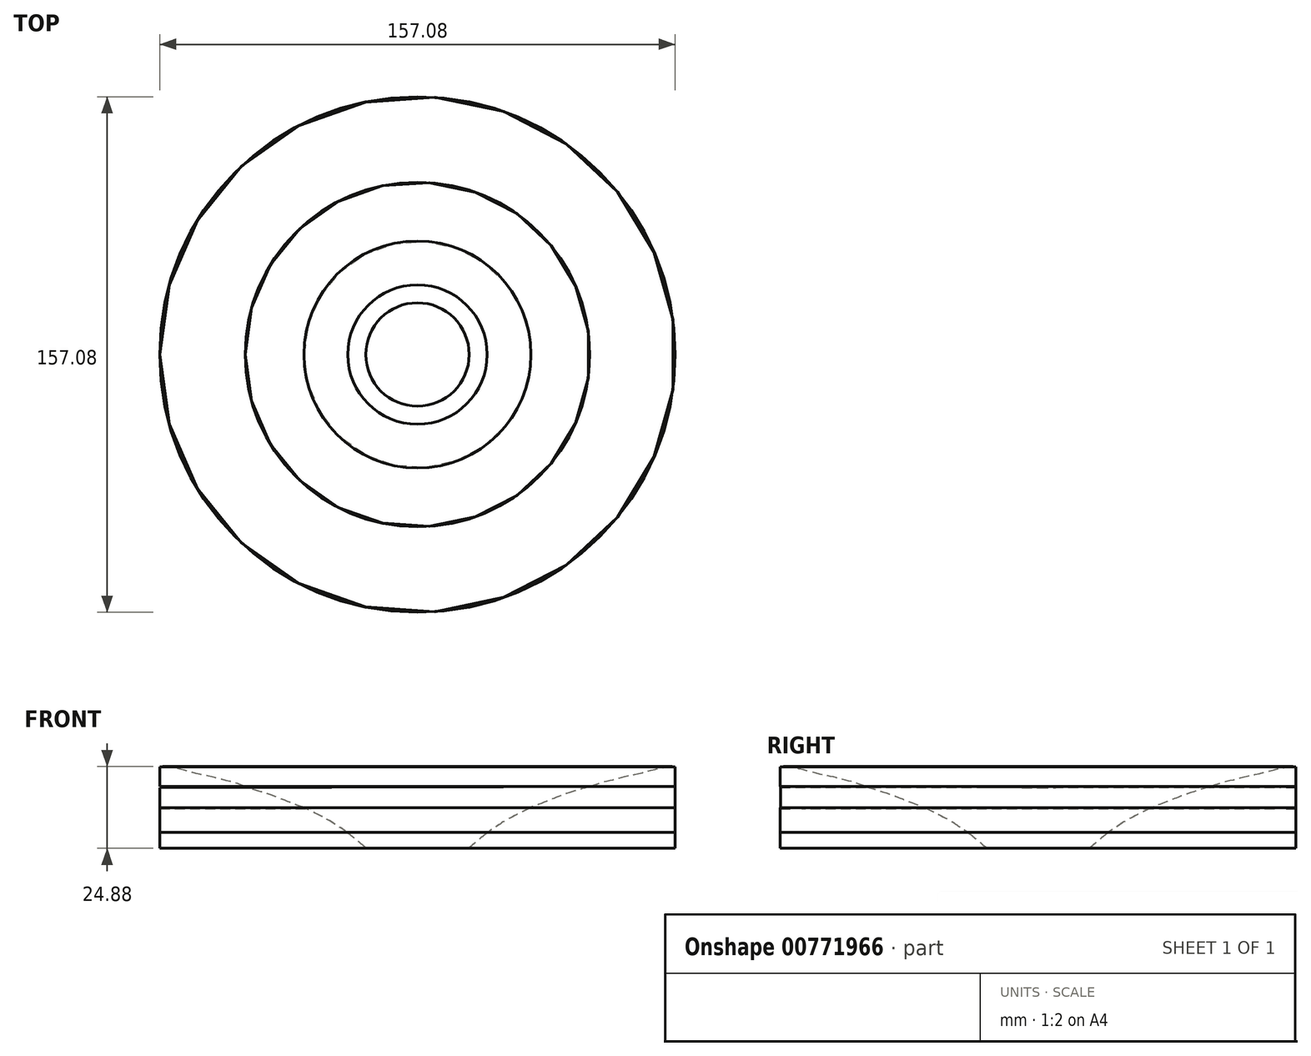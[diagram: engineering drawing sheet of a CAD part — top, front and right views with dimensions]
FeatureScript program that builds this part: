
annotation { "Feature Type Name" : "Feature", "Feature Type Description" : "" }
export const myFeature = defineFeature(function(context is Context, id is Id, definition is map)
    precondition{}
    {
        {
            var Q0;
            Q0=qCreatedBy(makeId("Front.planeOp"),FACE);
            var sketch = newSketch(context, id + "F0", { "sketchPlane" : qUnion([Q0])});
            skPoint(sketch, "E0", {"position": v(15.75, 1.52) * mm});
            skPoint(sketch, "E1", {"position": v(17.28, 2.83) * mm});
            skPoint(sketch, "E2", {"position": v(18.96, 4.19) * mm});
            skPoint(sketch, "E3", {"position": v(20.72, 5.64) * mm});
            skPoint(sketch, "E4", {"position": v(21.99, 6.59) * mm});
            skPoint(sketch, "E5", {"position": v(23.17, 7.4) * mm});
            skPoint(sketch, "E6", {"position": v(24.75, 8.44) * mm});
            skPoint(sketch, "E7", {"position": v(25.79, 9.17) * mm});
            skPoint(sketch, "E8", {"position": v(26.74, 9.75) * mm});
            skPoint(sketch, "E9", {"position": v(27.69, 10.3) * mm});
            skPoint(sketch, "E10", {"position": v(29.05, 10.98) * mm});
            skPoint(sketch, "E11", {"position": v(29.86, 11.47) * mm});
            skPoint(sketch, "E12", {"position": v(30.72, 11.79) * mm});
            skPoint(sketch, "E13", {"position": v(31.94, 12.42) * mm});
            skPoint(sketch, "E14", {"position": v(33.75, 13.28) * mm});
            skPoint(sketch, "E15", {"position": v(34.66, 13.78) * mm});
            skPoint(sketch, "E16", {"position": v(36.15, 14.46) * mm});
            skPoint(sketch, "E17", {"position": v(38, 15.14) * mm});
            skPoint(sketch, "E18", {"position": v(40, 15.95) * mm});
            skPoint(sketch, "E19", {"position": v(41.44, 16.5) * mm});
            skPoint(sketch, "E20", {"position": v(42.84, 17) * mm});
            skPoint(sketch, "E21", {"position": v(44.34, 17.63) * mm});
            skPoint(sketch, "E22", {"position": v(45.47, 18.03) * mm});
            skPoint(sketch, "E23", {"position": v(46.28, 18.26) * mm});
            skPoint(sketch, "E24", {"position": v(47.55, 18.9) * mm});
            skPoint(sketch, "E25", {"position": v(48.18, 18.98) * mm});
            skPoint(sketch, "E26", {"position": v(49.04, 19.3) * mm});
            skPoint(sketch, "E27", {"position": v(49.67, 19.34) * mm});
            skPoint(sketch, "E28", {"position": v(51.76, 20.16) * mm});
            skPoint(sketch, "E29", {"position": v(53.3, 20.48) * mm});
            skPoint(sketch, "E30", {"position": v(55.37, 20.84) * mm});
            skPoint(sketch, "E31", {"position": v(56.69, 21.6) * mm});
            skPoint(sketch, "E32", {"position": v(58.22, 21.88) * mm});
            skPoint(sketch, "E33", {"position": v(60.22, 22.42) * mm});
            skPoint(sketch, "E34", {"position": v(61.35, 22.6) * mm});
            skPoint(sketch, "E35", {"position": v(62.8, 23.14) * mm});
            skPoint(sketch, "E36", {"position": v(64.1, 23.5) * mm});
            skPoint(sketch, "E37", {"position": v(66.32, 23.87) * mm});
            skPoint(sketch, "E38", {"position": v(68.09, 24.23) * mm});
            skPoint(sketch, "E39", {"position": v(70.12, 24.82) * mm});
            skPoint(sketch, "E40", {"position": v(71.66, 25.09) * mm});
            skPoint(sketch, "E41", {"position": v(73.52, 25.68) * mm});
            skPoint(sketch, "E42", {"position": v(74.96, 25.95) * mm});
            skPoint(sketch, "E43", {"position": v(76.86, 26.18) * mm});
            skPoint(sketch, "E44", {"position": v(78.54, 26.72) * mm});
            skFitSpline(sketch, "E45", {"points": [v(15.75, 1.52) * mm, v(17.28, 2.83) * mm, v(18.96, 4.19) * mm, v(20.72, 5.64) * mm, v(21.99, 6.59) * mm, v(23.17, 7.4) * mm, v(24.75, 8.44) * mm, v(25.79, 9.17) * mm, v(29.05, 10.98) * mm, v(31.94, 12.42) * mm, v(34.66, 13.78) * mm, v(38, 15.14) * mm, v(41.44, 16.5) * mm, v(45.47, 18.03) * mm, v(49.67, 19.34) * mm, v(53.3, 20.48) * mm, v(56.69, 21.6) * mm, v(60.22, 22.42) * mm, v(62.8, 23.14) * mm, v(66.32, 23.87) * mm, v(70.12, 24.82) * mm, v(73.52, 25.68) * mm, v(76.86, 26.18) * mm, v(78.54, 26.18) * mm], "startDerivative": vector(41.71, 36.37) * mm, "endDerivative": vector(45.9, -1.96) * mm});
            skLineSegment(sketch, "E46", {"start": v(78.54, 26.18) * mm, "end": v(78.54, 1.32) * mm});
            skLineSegment(sketch, "E47", {"start": v(78.54, 1.32) * mm, "end": v(15.75, 1.52) * mm});
            skLineSegment(sketch, "E48", {"start": v(0, 1.5) * mm, "end": v(0, 31.45) * mm});
            skLineSegment(sketch, "E49", {"start": v(0, 1.5) * mm, "end": v(0.07, 1.5) * mm});
            skLineSegment(sketch, "E50", {"start": v(0.07, 1.5) * mm, "end": v(0, 31.45) * mm});
            skLineSegment(sketch, "E51", {"start": v(78.54, 6.17) * mm, "end": v(0, 5.99) * mm});
            skLineSegment(sketch, "E52", {"start": v(78.54, 13.75) * mm, "end": v(0, 13.75) * mm});
            skLineSegment(sketch, "E53", {"start": v(78.54, 20.21) * mm, "end": v(0, 20.21) * mm});
            skSolve(sketch);
        }
        {
            var Q0;
            {var subQ0=sQuery(id+"F0.wireOp",EDGE,"E47");Q0=makeQuery(id+"F0.imprint","IMPRINT",FACE,{"disambiguationData":[TD([[makeQuery(id+"F0.imprint","IMPRINT",EDGE,{"derivedFrom":subQ0}),-1.0]])]});}
            var Q1;
            Q1=sQuery(id+"F0.wireOp",EDGE,"E48");
            revolve(context, id + "F1", {"surfaceOperationType" : NewSurfaceOperationType.NEW, "entities" : qUnion([Q0]), "axis" : qUnion([Q1]), "revolveType" : RevolveType.FULL});
        }
        {
            var Q0;
            {var subQ0=sQuery(id+"F0.wireOp",EDGE,"E51");var subQ1=sQuery(id+"F0.wireOp",EDGE,"E45");var subQ2=makeQuery(id+"F0.imprint","INTERSECT",VERTEX,{"derivedFrom":[subQ1,subQ0]});Q0=makeQuery(id+"F0.imprint","IMPRINT",FACE,{"disambiguationData":[TD([[makeQuery(id+"F0.imprint","IMPRINT",EDGE,{"disambiguationData":[TD([[subQ2,-1.0]])],"derivedFrom":subQ1}),-1.0]])]});}
            var Q1;
            Q1=sQuery(id+"F0.wireOp",EDGE,"E48");
            revolve(context, id + "F2", {"surfaceOperationType" : NewSurfaceOperationType.NEW, "entities" : qUnion([Q0]), "axis" : qUnion([Q1]), "revolveType" : RevolveType.FULL});
        }
        {
            var Q0;
            {var subQ0=sQuery(id+"F0.wireOp",EDGE,"E53");var subQ1=sQuery(id+"F0.wireOp",EDGE,"E45");var subQ2=makeQuery(id+"F0.imprint","INTERSECT",VERTEX,{"derivedFrom":[subQ1,subQ0]});Q0=makeQuery(id+"F0.imprint","IMPRINT",FACE,{"disambiguationData":[TD([[makeQuery(id+"F0.imprint","IMPRINT",EDGE,{"disambiguationData":[TD([[subQ2,1.0]])],"derivedFrom":subQ1}),-1.0]])]});}
            var Q1;
            Q1=sQuery(id+"F0.wireOp",EDGE,"E50");
            revolve(context, id + "F3", {"surfaceOperationType" : NewSurfaceOperationType.NEW, "entities" : qUnion([Q0]), "axis" : qUnion([Q1]), "revolveType" : RevolveType.FULL});
        }
        {
            var Q0;
            {var subQ0=sQuery(id+"F0.wireOp",EDGE,"E46");var subQ1=sQuery(id+"F0.wireOp",EDGE,"E45");var subQ2=makeQuery(id+"F0.imprint","INTERSECT",VERTEX,{"derivedFrom":[subQ1,subQ0]});Q0=makeQuery(id+"F0.imprint","IMPRINT",FACE,{"disambiguationData":[TD([[makeQuery(id+"F0.imprint","IMPRINT",EDGE,{"disambiguationData":[TD([[subQ2,1.0]])],"derivedFrom":subQ1}),-1.0]])]});}
            var Q1;
            Q1=sQuery(id+"F0.wireOp",EDGE,"E48");
            revolve(context, id + "F4", {"surfaceOperationType" : NewSurfaceOperationType.NEW, "entities" : qUnion([Q0]), "axis" : qUnion([Q1]), "revolveType" : RevolveType.FULL});
        }
    });
